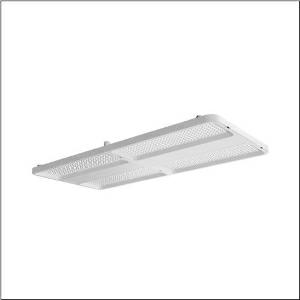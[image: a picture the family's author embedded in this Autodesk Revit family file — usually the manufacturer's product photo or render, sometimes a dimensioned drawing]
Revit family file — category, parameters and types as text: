
# Revit family: highbay_21_maxi_52hn12db4mda02
name_source: partatom
category: Lighting Fixtures
units: mm (PartAtom-declared; Revit-internal decimal feet)

## family parameters
Cut with Voids When Loaded = No
Host = Face
Light Source = No
Part Type = Normal
Room Calculation Point = No
Round Connector Dimension = Use Diameter
Shared = No

## types (1)
- --- (1 x LED, 28000 lm, 144.5 W, 4000K)
    Apparent Load = 144 VA
    CIE Flux Codes = 90 98 100 100 100
    Color Rendering = 80
    Color Temperature = 4000K
    Default Elevation = 1800 mm
    Description = high bay luminaire Highbay 21 maxi; direct symmetric wide distribution, light control with lens of PMMA; UGR ≤ 22 (X = 4H | Y = 8H | S = 0.25H | reflection values 70/50/20); luminous flux: 28.000lm; light colour: 840, colour temperature: 4000K, MacAdam ≤ 3 SDCM (initial), colour rendering: CRI > 80; luminous efficacy: 193,8lm/W; rated service life: 75.000h (L80/B50) at AT= ta max; control: Bluetooth® Mesh; for wireless networking: Node luminaire for setting up a local control solution without a higher-level application controller, intelligence completely in the luminaire; no control line such as DALI between the Node multi-sensor luminaires and Nodes is required, wireless integration of other Node luminaires and Node multi-sensor luminaires into the network is possible; number of Node luminaires in the project can be expanded as required, network sizes > 300 Nodes can be realized; can also be connected to lighting or building automation via various gateways upon request; integrated DALI2 ECG provides luminaire data (according to IEC62386, Part 251), energy data (Part 252), and monitoring and analytics data (Part 253) to higher-level systems for further processing; luminaire connection: terminal, 5-pole, max. 2.5mm² (cable entry for one cable, Ø 8.5..16mm); mains connection: 230..240V, AC 50/60Hz; connected load: 144,5W; protection rating (complete): IP66; insulation class (complete): insulation class I (protective earthing); protection symbol: D; impact resistance: IK08; certification: CE, ENEC, VDE, UKCA; internal wiring halogen-free; luminaire corresponds to IFS (International Featured Standards) requirements for safety and quality in the food industry; LABS conformity tested according to VDMA 24364:2018-05; housing frame of high-performance plastic PA6, matt traffic white (RAL 9016); cover of PMMA; dimension (LxWxH): 946 x 442 x 72mm; permissible operating ambient temperature: -20..+45°C (reducing of maximum allowable ambient temperature of 5°C with ceiling mounting); packaging unit: 1 piece; (delivery without accessories; please order mounting accessories separately)
    Height = 72 mm  [stored 0.23622 ft]
    Lamp = 1 x LED
    Lamp Light Flux = 28000 lm
    Lamp Power = 144.5 W
    Lamp count = 1
    Length = 946 mm
    Luminous efficacy = 194 lm/W
    Manufacturer = Siteco
    ModVariant = No
    Model = 52HN12DB4MDA02
    Mounting Place = Ceiling
    Mounting Type = Pendant
    Number of Poles = 1
    OnlyDefault = Yes
    Power Factor = 1
    Product Name = Highbay 21 maxi
    Product group = high bay luminaire
    ProductGroupID = 901
    Protection Class = Protection class I
    Protection Degree = IP 66
    RLX_Detail_Level = 1
    RLX_Emergency_Light_Flux = 0 lm
    RLX_Emergency_Type = 0
    RLX_Emergency_Type_DB = No
    RlxData = <blob elided: 128709 chars, md5=5b0c0638>
    Socket = socket
    Standby Power = 0 W
    System Light Flux = 28000 lm
    System Power = 144 W
    Type Comments = factory setting: luminous flux: 100 % | dim-lin: 254 | 668 mA
    Type Image = l_1363244.jpg
    URL = http://relux.com
    VarID = @adj_011829
    Voltage = 0 V
    Weight = 0.00 kg
    Width = 442 mm

note: [stored X ft] marks values corroborated as IEEE doubles in the binary element streams (Revit-internal decimal feet)

## geometry (parser evidence)
native form markers: Blend x4, Sweep x9
no freeform markers — native parametric forms only
